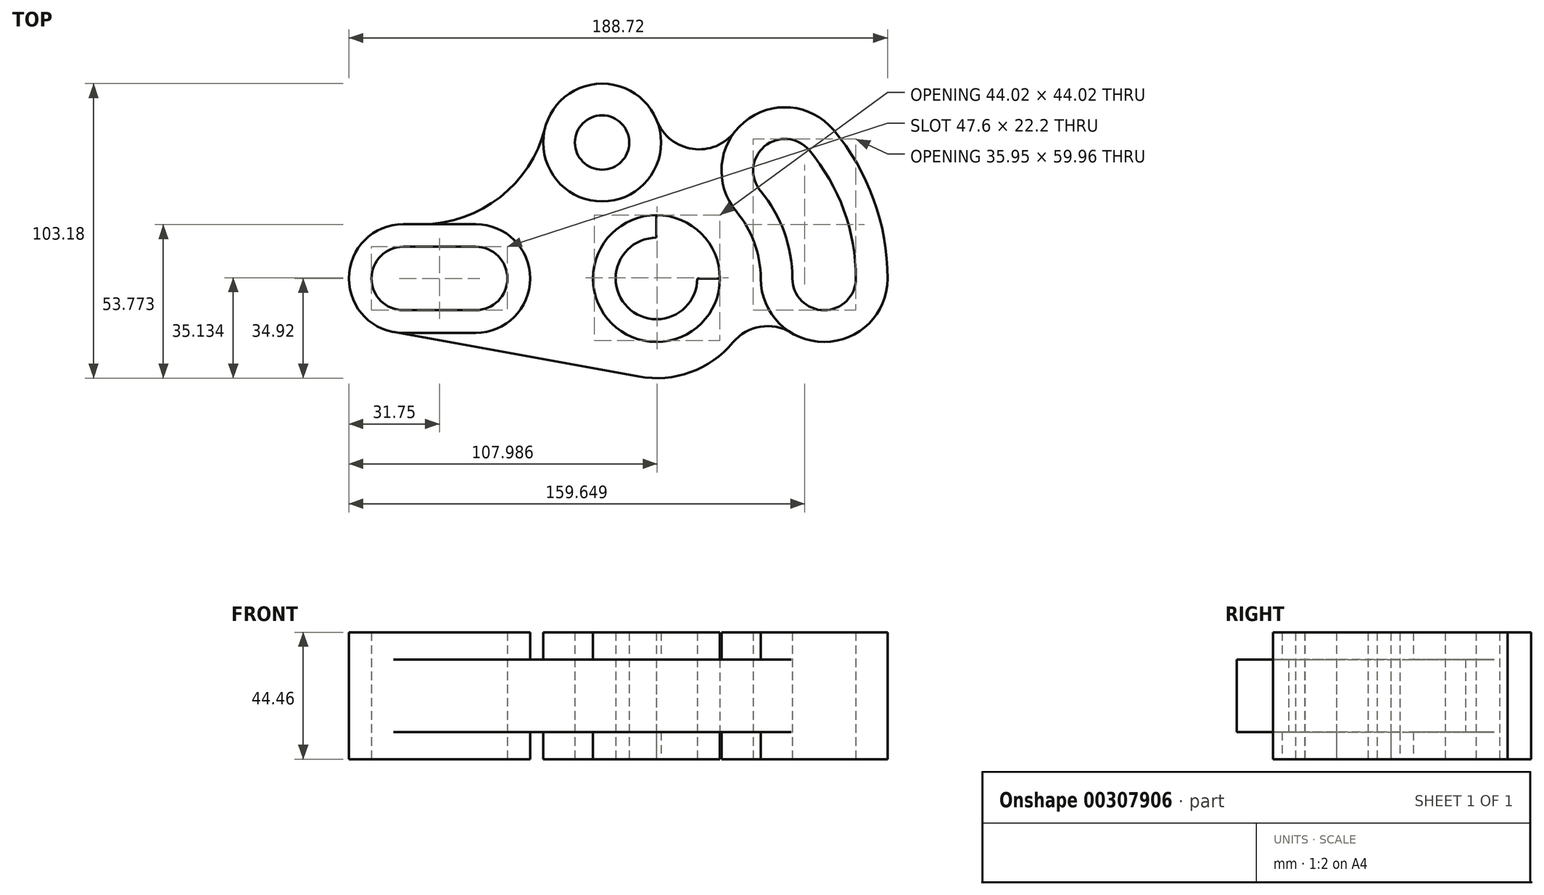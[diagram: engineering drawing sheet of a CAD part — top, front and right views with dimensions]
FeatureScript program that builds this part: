
annotation { "Feature Type Name" : "Feature", "Feature Type Description" : "" }
export const myFeature = defineFeature(function(context is Context, id is Id, definition is map)
    precondition{}
    {
        {
            var Q0;
            Q0=qCreatedBy(makeId("Top.planeOp"),FACE);
            var sketch = newSketch(context, id + "F0", { "sketchPlane" : qUnion([Q0])});
            skLineSegment(sketch, "E0", {"start": v(0, 0) * mm, "end": v(147.45, 0) * mm});
            skLineSegment(sketch, "E1", {"start": v(0, 0) * mm, "end": v(25.4, 0) * mm});
            skLineSegment(sketch, "E2", {"start": v(147.45, 0) * mm, "end": v(88.72, 0) * mm});
            skCircle(sketch, "E3", {"center": v(88.72, 0) * mm, "radius": 22.23 * mm});
            skCircle(sketch, "E4", {"center": v(88.72, 0) * mm, "radius": 14.29 * mm});
            skArc(sketch, "E5", {"start": v(0, 11.1) * mm, "mid": v(-11.1, 0) * mm, "end": v(0, -11.1) * mm});
            skArc(sketch, "E6", {"start": v(0, 19.05) * mm, "mid": v(-19.05, 0) * mm, "end": v(0, -19.05) * mm});
            skArc(sketch, "E7", {"start": v(25.4, -19.05) * mm, "mid": v(44.45, 0) * mm, "end": v(25.4, 19.05) * mm});
            skArc(sketch, "E8", {"start": v(25.4, -11.1) * mm, "mid": v(36.5, 0) * mm, "end": v(25.4, 11.1) * mm});
            skLineSegment(sketch, "E9", {"start": v(0, 19.05) * mm, "end": v(25.4, 19.05) * mm});
            skLineSegment(sketch, "E10", {"start": v(0, 11.1) * mm, "end": v(25.4, 11.1) * mm});
            skLineSegment(sketch, "E11", {"start": v(0, -11.1) * mm, "end": v(25.4, -11.1) * mm});
            skLineSegment(sketch, "E12", {"start": v(0, -19.05) * mm, "end": v(25.4, -19.05) * mm});
            skLineSegment(sketch, "E13", {"start": v(88.72, 0) * mm, "end": v(88.72, 47.63) * mm});
            skLineSegment(sketch, "E14", {"start": v(88.72, 47.63) * mm, "end": v(69.67, 47.63) * mm});
            skCircle(sketch, "E15", {"center": v(69.67, 47.63) * mm, "radius": 20.64 * mm});
            skCircle(sketch, "E16", {"center": v(69.67, 47.63) * mm, "radius": 9.53 * mm});
            skLineSegment(sketch, "E17", {"start": v(-3.4, -18.74) * mm, "end": v(85.61, -34.93) * mm});
            skArc(sketch, "E18", {"start": v(6.55, 19.05) * mm, "mid": v(33.88, 28.45) * mm, "end": v(49.66, 52.66) * mm});
            skLineSegment(sketch, "E19", {"start": v(88.72, 0) * mm, "end": v(184.06, 80) * mm, "construction": true});
            skArc(sketch, "E20", {"start": v(136.32, 0) * mm, "mid": v(147.45, -11.13) * mm, "end": v(158.57, 0) * mm});
            skArc(sketch, "E21", {"start": v(142.23, 44.9) * mm, "mid": v(126.56, 46.27) * mm, "end": v(125.19, 30.6) * mm});
            skArc(sketch, "E22", {"start": v(150.73, 52.03) * mm, "mid": v(119.42, 54.77) * mm, "end": v(116.68, 23.46) * mm});
            skArc(sketch, "E23", {"start": v(125.22, 0) * mm, "mid": v(123.02, 12.48) * mm, "end": v(116.68, 23.46) * mm});
            skArc(sketch, "E24", {"start": v(169.67, 0) * mm, "mid": v(164.8, 27.69) * mm, "end": v(150.73, 52.03) * mm});
            skArc(sketch, "E25", {"start": v(88.85, 55.24) * mm, "mid": v(101.38, 45.39) * mm, "end": v(116.15, 51.37) * mm});
            skArc(sketch, "E26", {"start": v(125.22, 0) * mm, "mid": v(147.45, -22.22) * mm, "end": v(169.67, 0) * mm});
            skLineSegment(sketch, "E27", {"start": v(147.45, 0) * mm, "end": v(169.67, 0) * mm});
            skArc(sketch, "E28", {"start": v(125.19, 30.6) * mm, "mid": v(133.45, 16.28) * mm, "end": v(136.32, 0) * mm});
            skArc(sketch, "E29", {"start": v(142.23, 44.9) * mm, "mid": v(154.36, 23.9) * mm, "end": v(158.57, 0) * mm});
            skArc(sketch, "E30", {"start": v(82.47, -34.36) * mm, "mid": v(100.6, -32.84) * mm, "end": v(115.52, -22.4) * mm});
            skArc(sketch, "E31", {"start": v(135.93, -19) * mm, "mid": v(125.1, -16.92) * mm, "end": v(115.52, -22.4) * mm});
            skSolve(sketch);
        }
        {
            var Q0;
            {var subQ3=sQuery(id+"F0.wireOp",EDGE,"E18");Q0=makeQuery(id+"F0.imprint","IMPRINT",FACE,{"disambiguationData":[TD([[makeQuery(id+"F0.imprint","IMPRINT",EDGE,{"derivedFrom":subQ3}),-1.0]])]});}
            var Q1;
            {var subQ0=sQuery(id+"F0.wireOp",EDGE,"E12");Q1=makeQuery(id+"F0.imprint","IMPRINT",FACE,{"disambiguationData":[TD([[makeQuery(id+"F0.imprint","IMPRINT",EDGE,{"derivedFrom":subQ0}),-1.0]])]});}
            var Q2;
            {var subQ6=sQuery(id+"F0.wireOp",EDGE,"E23");Q2=makeQuery(id+"F0.imprint","IMPRINT",FACE,{"disambiguationData":[TD([[makeQuery(id+"F0.imprint","IMPRINT",EDGE,{"derivedFrom":subQ6}),1.0]])]});}
            extrude(context, id + "F1", {"entities" : qUnion([Q0, Q1, Q2]), "depth" : 25.4 * mm, "symmetric" : true});
        }
        {
            var Q0;
            Q0=makeQuery(id+"F0.imprint","IMPRINT",FACE,{"disambiguationData":[TD([[makeQuery(id+"F0.imprint","IMPRINT",EDGE,{"derivedFrom":sQuery(id+"F0.wireOp",EDGE,"E5")}),-1.0]])]});
            var Q1;
            Q1=makeQuery(id+"F0.imprint","IMPRINT",FACE,{"disambiguationData":[TD([[makeQuery(id+"F0.imprint","IMPRINT",EDGE,{"derivedFrom":sQuery(id+"F0.wireOp",EDGE,"E16")}),-1.0]])]});
            var Q2;
            {var subQ0=sQuery(id+"F0.wireOp",EDGE,"E3");var subQ1=sQuery(id+"F0.wireOp",EDGE,"E0");var subQ2=makeQuery(id+"F0.imprint","INTERSECT",VERTEX,{"derivedFrom":[subQ1,subQ0]});Q2=makeQuery(id+"F0.imprint","IMPRINT",FACE,{"disambiguationData":[TD([[makeQuery(id+"F0.imprint","IMPRINT",EDGE,{"disambiguationData":[TD([[subQ2,-1.0]])],"derivedFrom":subQ1}),1.0]])]});}
            var Q3;
            {var subQ0=sQuery(id+"F0.wireOp",EDGE,"E3");var subQ1=sQuery(id+"F0.wireOp",EDGE,"E2");var subQ2=makeQuery(id+"F0.imprint","INTERSECT",VERTEX,{"derivedFrom":[subQ1,subQ0]});Q3=makeQuery(id+"F0.imprint","IMPRINT",FACE,{"disambiguationData":[TD([[makeQuery(id+"F0.imprint","IMPRINT",EDGE,{"disambiguationData":[TD([[subQ2,-1.0]])],"derivedFrom":subQ1}),-1.0]])]});}
            var Q4;
            {var subQ0=sQuery(id+"F0.wireOp",EDGE,"E3");var subQ1=sQuery(id+"F0.wireOp",EDGE,"E0");var subQ2=makeQuery(id+"F0.imprint","INTERSECT",VERTEX,{"derivedFrom":[subQ1,subQ0]});Q4=makeQuery(id+"F0.imprint","IMPRINT",FACE,{"disambiguationData":[TD([[makeQuery(id+"F0.imprint","IMPRINT",EDGE,{"disambiguationData":[TD([[subQ2,-1.0]])],"derivedFrom":subQ1}),-1.0]])]});}
            var Q5;
            {var subQ6=sQuery(id+"F0.wireOp",EDGE,"E20");Q5=makeQuery(id+"F0.imprint","IMPRINT",FACE,{"disambiguationData":[TD([[makeQuery(id+"F0.imprint","IMPRINT",EDGE,{"derivedFrom":subQ6}),-1.0]])]});}
            var Q6;
            Q6=makeQuery(id+"F0.imprint","IMPRINT",FACE,{"disambiguationData":[TD([[makeQuery(id+"F0.imprint","IMPRINT",EDGE,{"derivedFrom":sQuery(id+"F0.wireOp",EDGE,"E21")}),-1.0]])]});
            extrude(context, id + "F2", {"entities" : qUnion([Q0, Q1, Q2, Q3, Q4, Q5, Q6]), "operationType" : NewBodyOperationType.ADD, "depth" : 44.45 * mm, "symmetric" : true});
        }
    });
